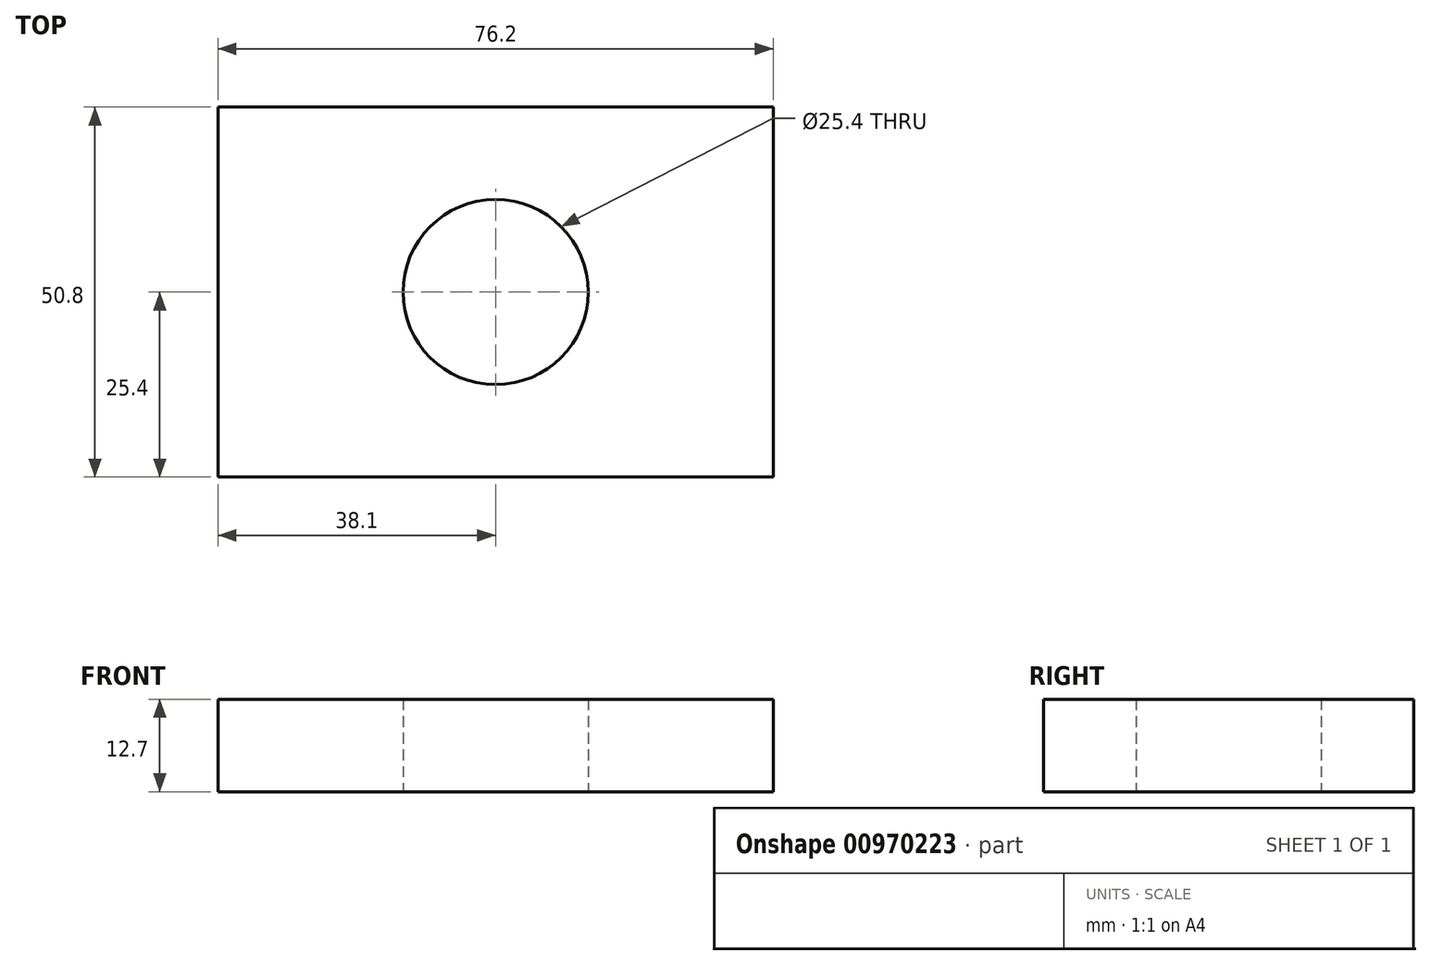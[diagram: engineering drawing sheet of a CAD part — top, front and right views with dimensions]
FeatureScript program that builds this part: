
annotation { "Feature Type Name" : "Feature", "Feature Type Description" : "" }
export const myFeature = defineFeature(function(context is Context, id is Id, definition is map)
    precondition{}
    {
        {
            var Q0;
            Q0=qCreatedBy(makeId("Top.planeOp"),FACE);
            var sketch = newSketch(context, id + "F0", { "sketchPlane" : qUnion([Q0])});
            skLineSegment(sketch, "E0.bottom", {"start": v(-38.1, 25.4) * mm, "end": v(38.1, 25.4) * mm});
            skLineSegment(sketch, "E0.top", {"start": v(-38.1, -25.4) * mm, "end": v(38.1, -25.4) * mm});
            skLineSegment(sketch, "E0.left", {"start": v(-38.1, 25.4) * mm, "end": v(-38.1, -25.4) * mm});
            skLineSegment(sketch, "E0.right", {"start": v(38.1, 25.4) * mm, "end": v(38.1, -25.4) * mm});
            skPoint(sketch, "E0.middle", {"position": v(0, 0) * mm});
            skCircle(sketch, "E1", {"center": v(0, 0) * mm, "radius": 12.7 * mm});
            skSolve(sketch);
        }
        {
            var Q0;
            Q0 = qSketchRegion(id + "F0", true);
            extrude(context, id + "F1", {"entities" : qUnion([Q0]), "depth" : 12.7 * mm, "offsetDistance" : 25.4 * mm});
        }
    });
